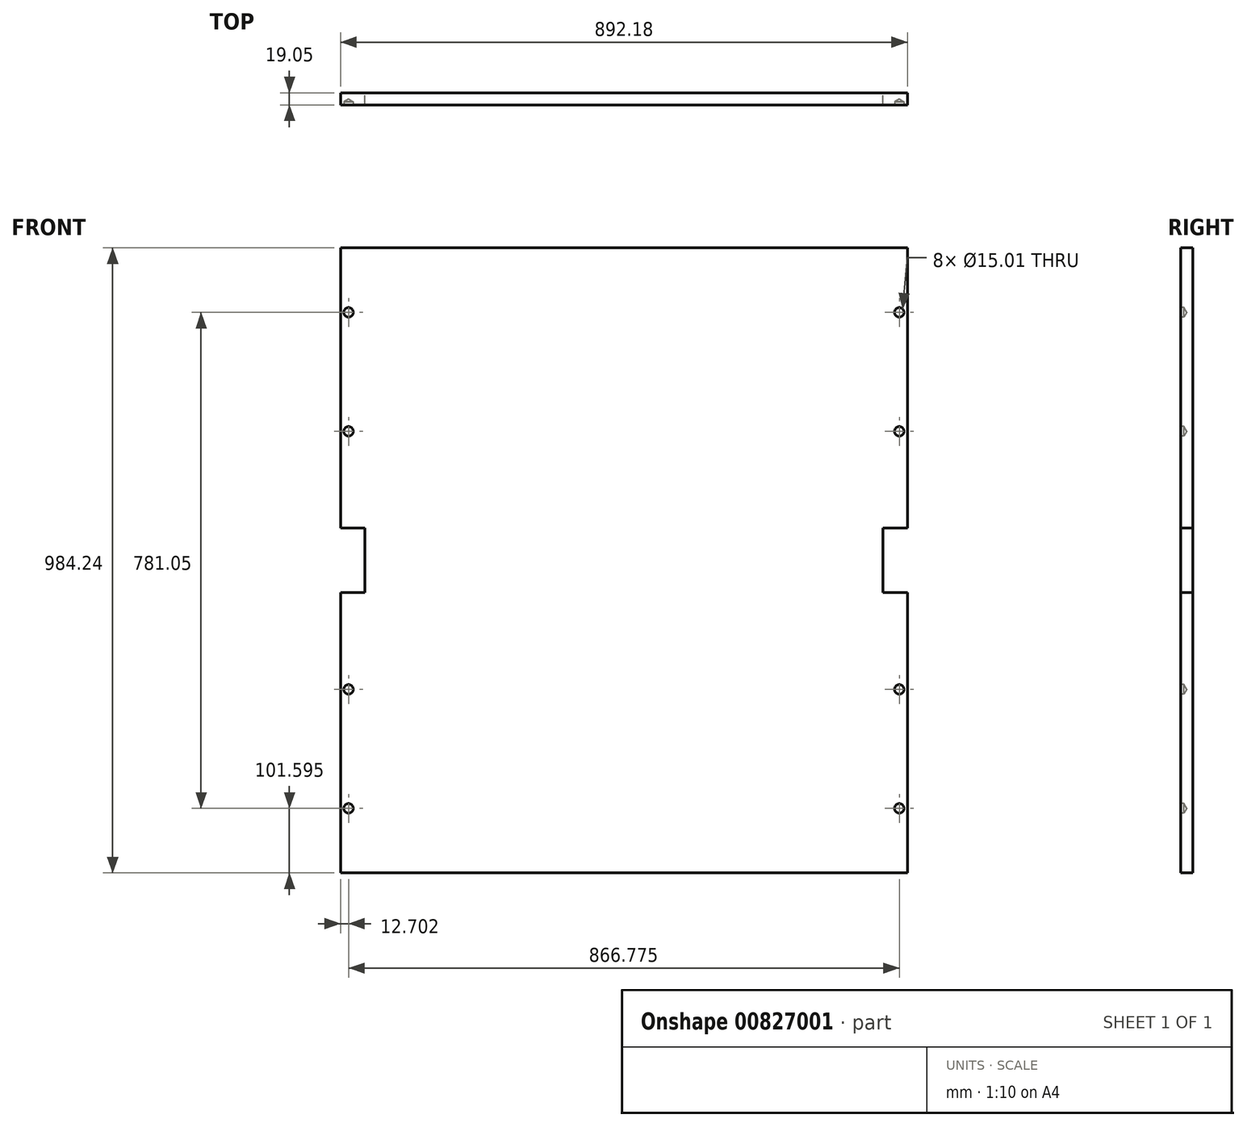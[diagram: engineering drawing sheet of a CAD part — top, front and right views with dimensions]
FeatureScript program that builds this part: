
annotation { "Feature Type Name" : "Feature", "Feature Type Description" : "" }
export const myFeature = defineFeature(function(context is Context, id is Id, definition is map)
    precondition{}
    {
        {
            var Q0;
            Q0=qCreatedBy(makeId("Front.planeOp"),FACE);
            var sketch = newSketch(context, id + "F0", { "sketchPlane" : qUnion([Q0])});
            skLineSegment(sketch, "E0.bottom", {"start": v(446.09, 492.12) * mm, "end": v(-446.09, 492.13) * mm});
            skLineSegment(sketch, "E0.top", {"start": v(446.09, -492.13) * mm, "end": v(-446.09, -492.12) * mm});
            skLineSegment(sketch, "E0.left", {"start": v(446.09, 492.12) * mm, "end": v(446.09, -492.12) * mm});
            skLineSegment(sketch, "E0.right", {"start": v(-446.09, 492.13) * mm, "end": v(-446.09, -492.13) * mm});
            skPoint(sketch, "E0.middle", {"position": v(0, 0) * mm});
            skLineSegment(sketch, "E1.bottom", {"start": v(-407.99, 50.8) * mm, "end": v(-484.19, 50.8) * mm});
            skLineSegment(sketch, "E1.top", {"start": v(-407.99, -50.8) * mm, "end": v(-484.19, -50.8) * mm});
            skLineSegment(sketch, "E1.left", {"start": v(-407.99, 50.8) * mm, "end": v(-407.99, -50.8) * mm});
            skLineSegment(sketch, "E1.right", {"start": v(-484.19, 50.8) * mm, "end": v(-484.19, -50.8) * mm});
            skPoint(sketch, "E1.middle", {"position": v(-446.09, 0) * mm});
            skLineSegment(sketch, "E2.bottom", {"start": v(407.99, 50.8) * mm, "end": v(484.19, 50.8) * mm});
            skLineSegment(sketch, "E2.top", {"start": v(407.99, -50.8) * mm, "end": v(484.19, -50.8) * mm});
            skLineSegment(sketch, "E2.left", {"start": v(407.99, 50.8) * mm, "end": v(407.99, -50.8) * mm});
            skLineSegment(sketch, "E2.right", {"start": v(484.19, 50.8) * mm, "end": v(484.19, -50.8) * mm});
            skPoint(sketch, "E2.middle", {"position": v(446.09, 0) * mm});
            skSolve(sketch);
        }
        {
            var Q0;
            {var subQ11=sQuery(id+"F0.wireOp",EDGE,"E0.bottom");Q0=makeQuery(id+"F0.imprint","IMPRINT",FACE,{"disambiguationData":[TD([[makeQuery(id+"F0.imprint","IMPRINT",EDGE,{"derivedFrom":subQ11}),1.0]])]});}
            extrude(context, id + "F1", {"entities" : qUnion([Q0]), "depth" : 19.05 * mm, "offsetDistance" : 25.4 * mm});
        }
        {
            var Q0;
            Q0=makeQuery(id+"F1.opExtrude","CAP_FACE",FACE,{"disambiguationData":[OSD([sQuery(id+"F0.wireOp",EDGE,"E0.bottom"),sQuery(id+"F0.wireOp",EDGE,"E0.top"),sQuery(id+"F0.wireOp",EDGE,"E0.left"),sQuery(id+"F0.wireOp",EDGE,"E0.right"),sQuery(id+"F0.wireOp",EDGE,"E1.bottom"),sQuery(id+"F0.wireOp",EDGE,"E1.top"),sQuery(id+"F0.wireOp",EDGE,"E1.left"),sQuery(id+"F0.wireOp",EDGE,"E2.bottom"),sQuery(id+"F0.wireOp",EDGE,"E2.top"),sQuery(id+"F0.wireOp",EDGE,"E2.left")])],"isStart":false});
            var sketch = newSketch(context, id + "F2", { "sketchPlane" : qUnion([Q0])});
            skLineSegment(sketch, "E3", {"start": v(-446.09, 492.13) * mm, "end": v(-433.39, 492.13) * mm});
            skLineSegment(sketch, "E4", {"start": v(-433.39, 492.13) * mm, "end": v(-433.39, 390.53) * mm});
            skLineSegment(sketch, "E5", {"start": v(446.09, 492.13) * mm, "end": v(433.39, 492.13) * mm});
            skLineSegment(sketch, "E6", {"start": v(433.39, 492.12) * mm, "end": v(433.39, 390.52) * mm});
            skLineSegment(sketch, "E7", {"start": v(-446.09, -492.12) * mm, "end": v(-433.39, -492.12) * mm});
            skLineSegment(sketch, "E8", {"start": v(-433.39, -492.12) * mm, "end": v(-433.39, -390.53) * mm});
            skLineSegment(sketch, "E9", {"start": v(446.09, -492.12) * mm, "end": v(433.39, -492.12) * mm});
            skLineSegment(sketch, "E10", {"start": v(433.39, -492.13) * mm, "end": v(433.39, -390.53) * mm});
            skLineSegment(sketch, "E11", {"start": v(-446.09, -50.8) * mm, "end": v(-446.09, -203.2) * mm});
            skLineSegment(sketch, "E12", {"start": v(-446.09, -203.2) * mm, "end": v(-433.39, -203.2) * mm});
            skLineSegment(sketch, "E13", {"start": v(-446.09, 50.8) * mm, "end": v(-446.09, 203.2) * mm});
            skLineSegment(sketch, "E14", {"start": v(-446.09, 203.2) * mm, "end": v(-433.39, 203.2) * mm});
            skLineSegment(sketch, "E15", {"start": v(446.09, 50.8) * mm, "end": v(446.09, 203.2) * mm});
            skLineSegment(sketch, "E16", {"start": v(446.09, 203.2) * mm, "end": v(433.39, 203.2) * mm});
            skLineSegment(sketch, "E17", {"start": v(446.09, -50.8) * mm, "end": v(446.09, -203.2) * mm});
            skLineSegment(sketch, "E18", {"start": v(446.09, -203.2) * mm, "end": v(433.39, -203.2) * mm});
            skPoint(sketch, "E19", {"position": v(-433.39, 390.53) * mm});
            skPoint(sketch, "E20", {"position": v(433.39, 390.52) * mm});
            skPoint(sketch, "E21", {"position": v(-433.39, 203.2) * mm});
            skPoint(sketch, "E22", {"position": v(433.39, 203.2) * mm});
            skPoint(sketch, "E23", {"position": v(433.39, -203.2) * mm});
            skPoint(sketch, "E24", {"position": v(-433.39, -203.2) * mm});
            skPoint(sketch, "E25", {"position": v(-433.39, -390.53) * mm});
            skPoint(sketch, "E26", {"position": v(433.39, -390.53) * mm});
            skSolve(sketch);
        }
        {
            var Q0;
            Q0=sQuery(id+"F2.wireOp",VERTEX,"E19");
            var Q1;
            Q1=sQuery(id+"F2.wireOp",VERTEX,"E21");
            var Q2;
            Q2=sQuery(id+"F2.wireOp",VERTEX,"E24");
            var Q3;
            Q3=sQuery(id+"F2.wireOp",VERTEX,"E25");
            var Q4;
            Q4=sQuery(id+"F2.wireOp",VERTEX,"E20");
            var Q5;
            Q5=sQuery(id+"F2.wireOp",VERTEX,"E22");
            var Q6;
            Q6=sQuery(id+"F2.wireOp",VERTEX,"E23");
            var Q7;
            Q7=sQuery(id+"F2.wireOp",VERTEX,"E26");
            var Q8;
            Q8=makeQuery(id+"F1.opExtrude","SWEPT_BODY",BODY,{"disambiguationData":[OSD([sQuery(id+"F0.wireOp",EDGE,"E0.bottom"),sQuery(id+"F0.wireOp",EDGE,"E0.top"),sQuery(id+"F0.wireOp",EDGE,"E0.left"),sQuery(id+"F0.wireOp",EDGE,"E0.right"),sQuery(id+"F0.wireOp",EDGE,"E1.bottom"),sQuery(id+"F0.wireOp",EDGE,"E1.top"),sQuery(id+"F0.wireOp",EDGE,"E1.left"),sQuery(id+"F0.wireOp",EDGE,"E2.bottom"),sQuery(id+"F0.wireOp",EDGE,"E2.top"),sQuery(id+"F0.wireOp",EDGE,"E2.left")])]});
            hole(context, id + "F3", {"style" : HoleStyle.SIMPLE, "endStyle" : HoleEndStyle.BLIND, "holeDiameter" : 15 * mm, "majorDiameter" : 6.35 * mm, "holeDepth" : 4.83 * mm, "isTappedThrough" : true, "tappedDepth" : 12.7 * mm, "tapClearance" : 3, "startFromSketch" : true, "locations" : qUnion([Q0, Q1, Q2, Q3, Q4, Q5, Q6, Q7]), "scope" : qUnion([Q8])});
        }
    });
